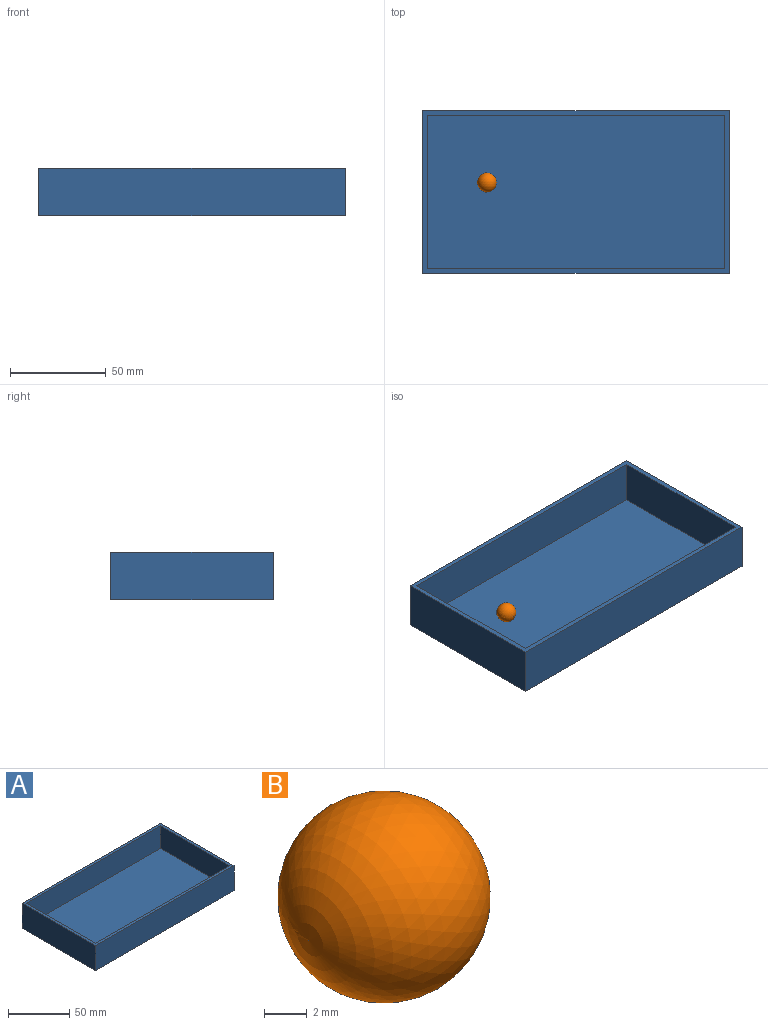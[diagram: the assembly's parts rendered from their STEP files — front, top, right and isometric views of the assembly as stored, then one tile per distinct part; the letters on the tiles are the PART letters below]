
ASSEMBLY  parts=2 mates=1
PART A: 11 faces, bbox 160x85x25 mm
  f0: plane 160x85mm, normal (0,0,1), area 1200mm2, adj f1,f2,f3,f4,f6,f7,f8,f9
  f1: plane 85x25mm, normal (1,0,0), area 2125mm2, adj f0,f2,f4,f5
  f2: plane 160x25mm, normal (0,1,0), area 4000mm2, adj f0,f1,f3,f5
  f3: plane 85x25mm, normal (-1,0,0), area 2125mm2, adj f0,f2,f4,f5
  f4: plane 160x25mm, normal (0,-1,0), area 4000mm2, adj f0,f1,f3,f5
  f5: plane 160x85mm, normal (0,0,-1), area 13600mm2, adj f1,f2,f3,f4
  f6: plane 80x22.5mm, normal (-1,0,0), area 1800mm2, adj f0,f7,f9,f10
  f7: plane 155x22.5mm, normal (0,-1,0), area 3487.5mm2, adj f0,f6,f8,f10
  f8: plane 80x22.5mm, normal (1,0,0), area 1800mm2, adj f0,f7,f9,f10
  f9: plane 155x22.5mm, normal (0,1,0), area 3487.5mm2, adj f0,f6,f8,f10
  f10: plane 155x80mm, normal (0,0,1), area 12400mm2, adj f6,f7,f8,f9
PART B: 1 faces, bbox 10x10x10 mm
  f0: sphere r=5mm, area 314.2mm2
PLACE A at identity fixed
PLACE B rot(axis=(0,0,1),90deg) t=(-147.51,59.48,10)mm
MATE planar A.f10 <-> B.f0  axis (0,0,1) through (0,0,2.5)mm
